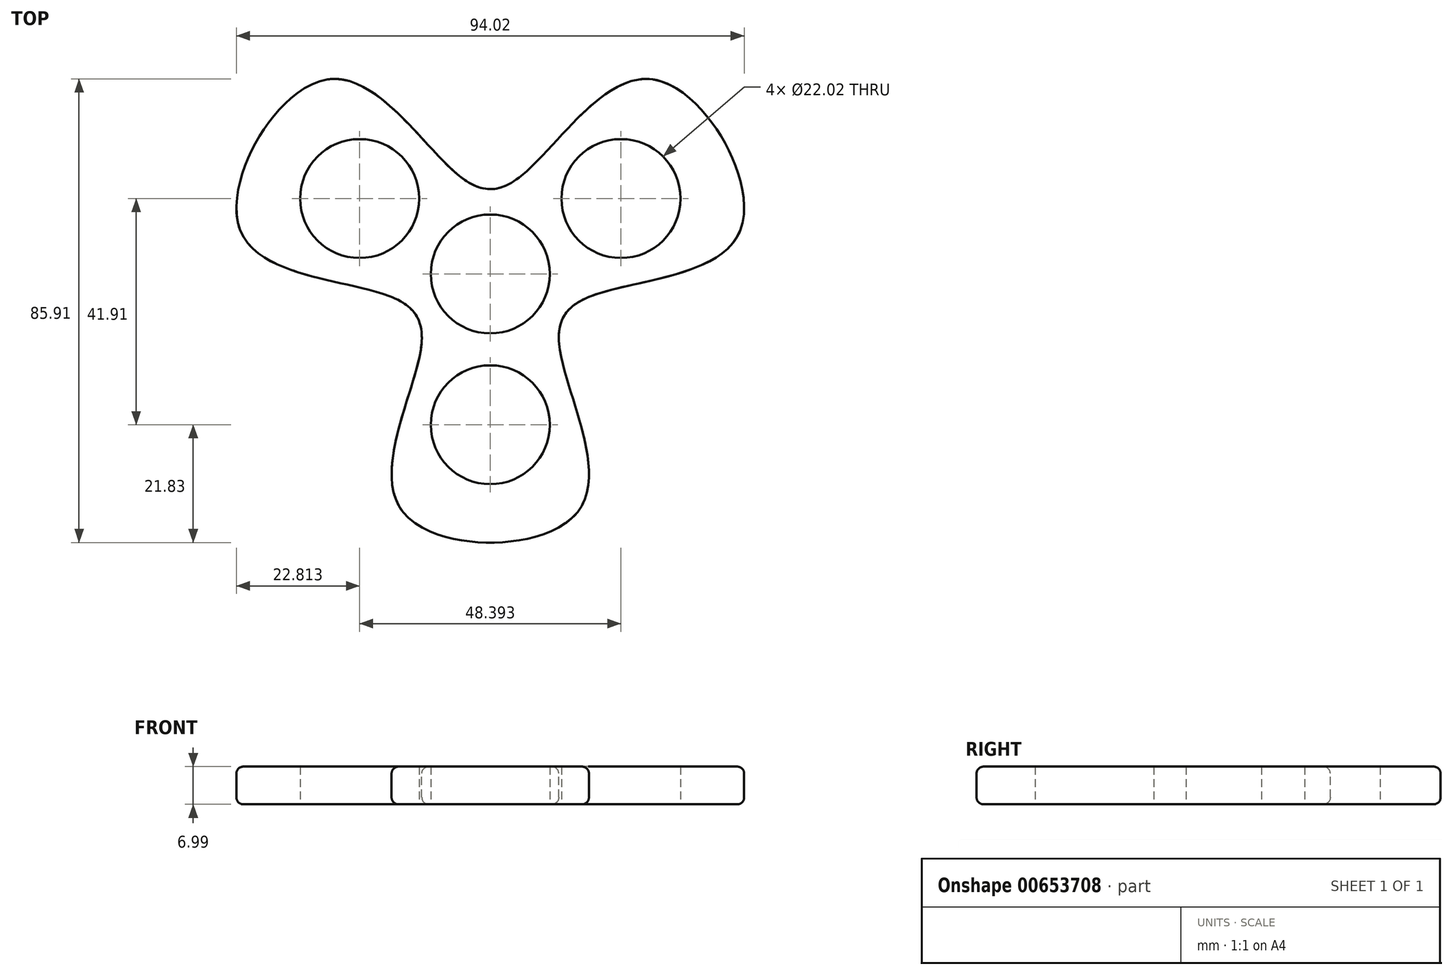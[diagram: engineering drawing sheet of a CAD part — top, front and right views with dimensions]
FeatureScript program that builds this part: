
annotation { "Feature Type Name" : "Feature", "Feature Type Description" : "" }
export const myFeature = defineFeature(function(context is Context, id is Id, definition is map)
    precondition{}
    {
        {
            var Q0;
            Q0=qCreatedBy(makeId("Top.planeOp"),FACE);
            var sketch = newSketch(context, id + "F0", { "sketchPlane" : qUnion([Q0])});
            skFitSpline(sketch, "E0", {"points": [v(-30.11, 36.05) * mm, v(-5.73, 18.17) * mm, v(5.73, 18.17) * mm, v(30.11, 36.05) * mm, v(46.28, 8.05) * mm, v(18.6, -4.12) * mm, v(12.87, -14.05) * mm, v(16.16, -44.1) * mm, v(-16.16, -44.1) * mm, v(-12.87, -14.05) * mm, v(-18.6, -4.12) * mm, v(-46.28, 8.05) * mm, v(-30.11, 36.05) * mm]});
            skCircle(sketch, "E1", {"center": v(-24.2, 13.97) * mm, "radius": 11.01 * mm});
            skCircle(sketch, "E2", {"center": v(24.2, 13.97) * mm, "radius": 11.01 * mm});
            skCircle(sketch, "E3", {"center": v(0, -27.94) * mm, "radius": 11.01 * mm});
            skCircle(sketch, "E4", {"center": v(0, 0) * mm, "radius": 11.01 * mm});
            skLineSegment(sketch, "E5", {"start": v(-24.2, 13.97) * mm, "end": v(0, 0) * mm});
            skLineSegment(sketch, "E6", {"start": v(0, 0) * mm, "end": v(24.2, 13.97) * mm});
            skLineSegment(sketch, "E7", {"start": v(0, 0) * mm, "end": v(0, -27.94) * mm});
            skLineSegment(sketch, "E8", {"start": v(-24.2, 13.97) * mm, "end": v(-30.11, 36.05) * mm});
            skLineSegment(sketch, "E9", {"start": v(-24.2, 13.97) * mm, "end": v(-46.28, 8.05) * mm});
            skLineSegment(sketch, "E10", {"start": v(0, -27.94) * mm, "end": v(-16.16, -44.1) * mm});
            skLineSegment(sketch, "E11", {"start": v(0, -27.94) * mm, "end": v(16.16, -44.1) * mm});
            skLineSegment(sketch, "E12", {"start": v(24.2, 13.97) * mm, "end": v(30.11, 36.05) * mm});
            skLineSegment(sketch, "E13", {"start": v(24.2, 13.97) * mm, "end": v(46.28, 8.05) * mm});
            skLineSegment(sketch, "E14", {"start": v(-12.87, -14.05) * mm, "end": v(0, 0) * mm});
            skLineSegment(sketch, "E15", {"start": v(0, 0) * mm, "end": v(-18.6, -4.12) * mm});
            skLineSegment(sketch, "E16", {"start": v(0, 0) * mm, "end": v(12.87, -14.05) * mm});
            skLineSegment(sketch, "E17", {"start": v(0, 0) * mm, "end": v(18.6, -4.12) * mm});
            skLineSegment(sketch, "E18", {"start": v(0, 0) * mm, "end": v(-5.73, 18.17) * mm});
            skLineSegment(sketch, "E19", {"start": v(0, 0) * mm, "end": v(5.73, 18.17) * mm});
            skSolve(sketch);
        }
        {
            var Q0;
            Q0 = qSketchRegion(id + "F0", true);
            extrude(context, id + "F1", {"entities" : qUnion([Q0]), "depth" : 7 * mm, "offsetDistance" : 25.4 * mm});
        }
        {
            var Q0;
            Q0=makeQuery(id+"F1.opExtrude","CAP_EDGE",EDGE,{"disambiguationData":[OSD([sQuery(id+"F0.wireOp",EDGE,"E0")])],"isStart":false});
            var Q1;
            Q1=makeQuery(id+"F1.opExtrude","CAP_EDGE",EDGE,{"disambiguationData":[OSD([sQuery(id+"F0.wireOp",EDGE,"E0")])],"isStart":true});
            fillet(context, id + "F2", {"entities" : qUnion([Q0, Q1]), "radius" : 1.27 * mm, "tangentPropagation" : true, "allowEdgeOverflow" : false});
        }
    });
